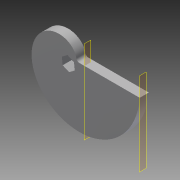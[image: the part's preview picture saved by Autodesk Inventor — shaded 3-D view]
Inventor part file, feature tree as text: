
AUTODESK INVENTOR PART (.ipt)
format: ipt  version: 2014 (Build 180170000, 170)  size: 151,552 bytes
history: native  units: in
note: dims shown in document units (in); Inventor stores cm internally (conversion verified against a paired STEP export)
features: extrude x2, plane x2, sketch x2, fillet x1, other x1
ambient origin geometry x8: Origin, YZ Plane, XZ Plane, XY Plane, X Axis, Y Axis, Z Axis, Center Point
bodies: Solid1 (feature_tree)
feature tree (8):
  extrude  "Extrusion1"  Depth=0.25in
  fillet  "Fillet1"  Radius=0.5in
  plane  "Work Plane2"
  extrude  "Extrusion2"  Depth=1.0in
  sketch  "Sketch1"  dims[d0=1.7235in d1=2.3684in d7=0.25in d9=0.5in]
  other  "2D Equation Curve1"
  plane  "Work Plane1"
  sketch  "Sketch2"  dims[d10=0.6654in d11=8.4985in d12=2.17in d13=2.9281in d14=0.375in d15=0.0in d16=0.125in d17=-2.27in d18=1.5in d19=1.25in d20=0.75in d21=0.5in d22=30.0deg d23=0.75in d24=0.1718in d25=1.0in d26=1.25in d27=1.625in d28=0.1718in d29=1.0in d30=0.0in]
